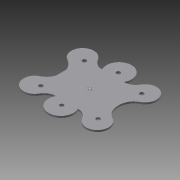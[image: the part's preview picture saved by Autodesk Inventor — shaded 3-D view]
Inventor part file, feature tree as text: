
AUTODESK INVENTOR PART (.ipt)
format: ipt  version: 2015 (Build 190159000, 159)  size: 168,960 bytes
history: native  units: in
note: dims shown in document units (in); Inventor stores cm internally (conversion verified against a paired STEP export)
features: sketch x13, extrude x7, plane x1, pattern_circular x1
ambient origin geometry x8: Origin, YZ Plane, XZ Plane, XY Plane, X Axis, Y Axis, Z Axis, Center Point
bodies: Solid1 (feature_tree)
feature tree (22):
  plane  "Work Plane1"
  extrude  "Extrusion1"  Depth=0.0984in
  sketch  "Sketch2"  dims[d13=0.1437in d14=0.0in d15=3.4611in]
  sketch  "Sketch4"  dims[d16=0.2362in d17=0.1437in d18=0.0in]
  extrude  "Extrusion5"  Depth=3.4611in
  extrude  "Extrusion6"  Depth=0.1437in TaperAngle=0.0deg
  sketch  "Sketch9"  dims[d44=0.2362in d45=0.3937in d46=0.0in]
  extrude  "Extrusion7"  Depth=0.1688in TaperAngle=0.0deg
  sketch  "Sketch22"
  sketch  "Sketch24"
  pattern_circular  "Circular Pattern1"  Count=6 Angle=360.0deg
  sketch  "Sketch25"
  extrude  "Extrusion8"  Depth=0.3937in TaperAngle=0.0deg
  extrude  "Extrusion9"  Depth=0.3937in TaperAngle=0.0deg
  extrude  "Extrusion10"  Depth=0.3937in TaperAngle=0.0deg
  sketch  "Sketch1"  dims[d1=0.0984in d2=0.0in d12=0.2362in]
  sketch  "Sketch7"  dims[d34=0.2362in d35=0.1688in d36=0.0in d38=2.3622in d39=360.0deg]
  sketch  "Sketch8"  dims[d41=0.2362in d42=0.3937in d43=0.0in]
  sketch  "Sketch21"  dims[d47=0.2362in d48=0.3937in d49=0.0in]
  sketch  "Sketch26"
  sketch  "Sketch27"
  sketch  "Sketch28"
